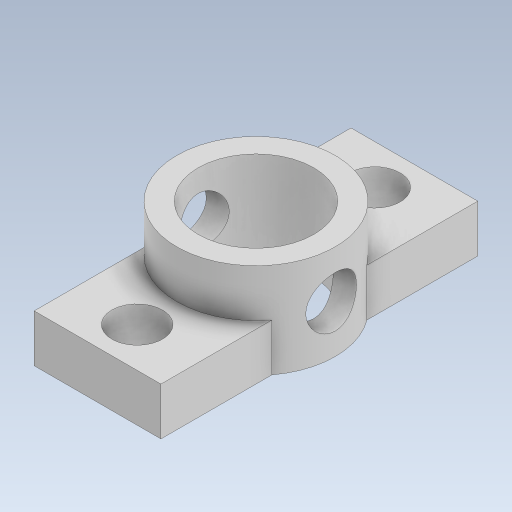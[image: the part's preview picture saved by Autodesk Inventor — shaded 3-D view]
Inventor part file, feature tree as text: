
AUTODESK INVENTOR PART (.ipt)
format: ipt  version: 2023.5 (Build 275446000, 446)  size: 160,256 bytes
history: native  units: mm
features: extrude x3, sketch x2, plane x1
ambient origin geometry x8: Origin, YZ Plane, XZ Plane, XY Plane, X Axis, Y Axis, Z Axis, Center Point
bodies: Solid1 (feature_tree)
feature tree (6):
  sketch  "Sketch1"  dims[d0=7.3mm d1=10.0mm]
  extrude  "Extrusion1"  Depth=10.0mm
  extrude  "Extrusion2"  Depth=10.0mm
  plane  "Work Plane1"
  extrude  "Extrusion3"  Depth=10.0mm
  sketch  "Sketch2"  dims[d2=20.0mm d3=3.2mm d4=2.5mm d5=3.2mm d6=2.5mm d7=3.0mm d8=0.0mm d9=6.0mm d10=0.0mm d11=3.2mm d12=10.0mm d13=0.0mm d14=0.5mm d15=0.872665mm d16=0.5mm d17=0.872665mm]
